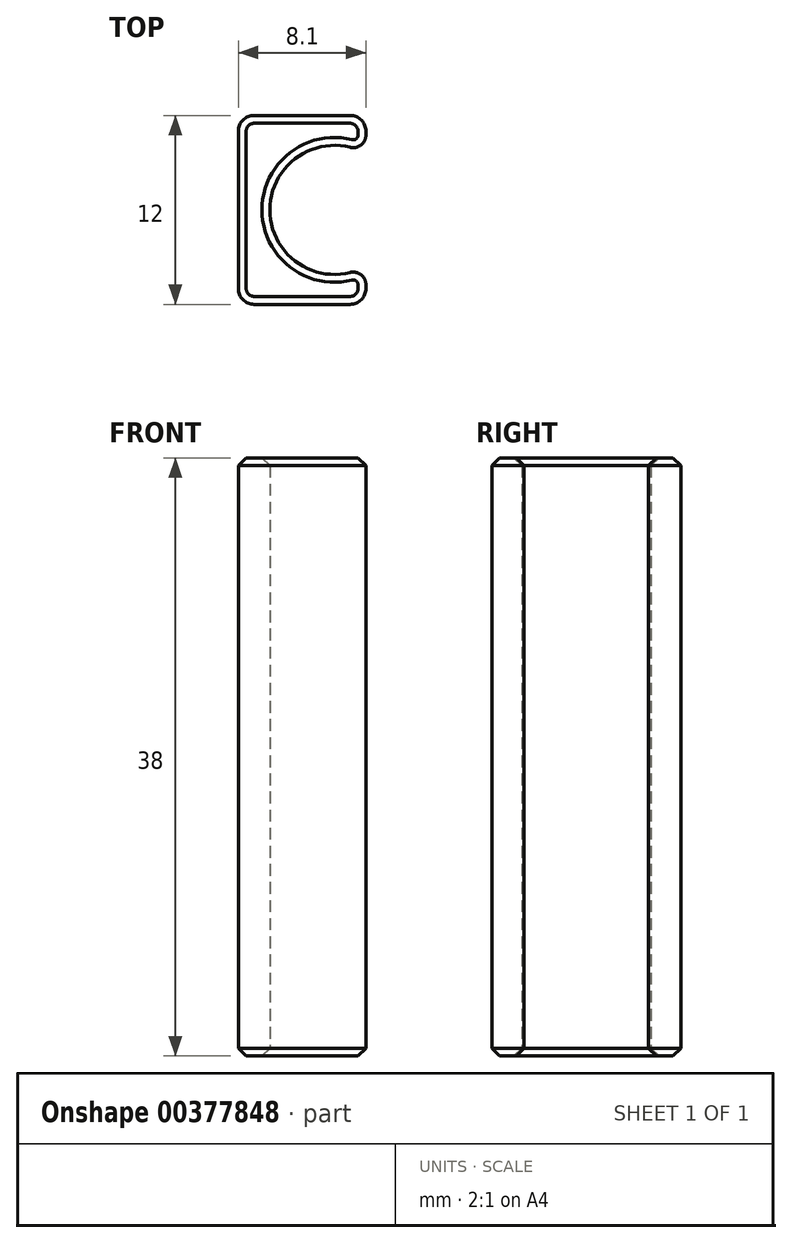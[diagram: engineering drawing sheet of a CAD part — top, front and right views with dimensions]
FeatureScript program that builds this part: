
annotation { "Feature Type Name" : "Feature", "Feature Type Description" : "" }
export const myFeature = defineFeature(function(context is Context, id is Id, definition is map)
    precondition{}
    {
        {
            var Q0;
            Q0=qCreatedBy(makeId("Top.planeOp"),FACE);
            var sketch = newSketch(context, id + "F0", { "sketchPlane" : qUnion([Q0])});
            skLineSegment(sketch, "E0.bottom", {"start": v(4.05, -6) * mm, "end": v(-4.05, -6) * mm});
            skLineSegment(sketch, "E0.top", {"start": v(4.05, 6) * mm, "end": v(-4.05, 6) * mm});
            skLineSegment(sketch, "E0.left", {"start": v(4.05, -6) * mm, "end": v(4.05, -3.58) * mm});
            skLineSegment(sketch, "E0.right", {"start": v(-4.05, -6) * mm, "end": v(-4.05, 6) * mm});
            skPoint(sketch, "E0.middle", {"position": v(0, 0) * mm});
            skArc(sketch, "E1", {"start": v(4.05, 3.58) * mm, "mid": v(-2.05, 0) * mm, "end": v(4.05, -3.58) * mm});
            skPoint(sketch, "E2", {"position": v(4.05, 0) * mm});
            skLineSegment(sketch, "E3.trimOffspring", {"start": v(4.05, 3.58) * mm, "end": v(4.05, 6) * mm});
            skSolve(sketch);
        }
        {
            var Q0;
            Q0 = qSketchRegion(id + "F0", true);
            extrude(context, id + "F1", {"entities" : qUnion([Q0]), "depth" : 38 * mm});
        }
        {
            var Q0;
            Q0=makeQuery(id+"F1.opExtrude","SWEPT_EDGE",EDGE,{"disambiguationData":[OSD([sQuery(id+"F0.wireOp",EDGE,"E1"),sQuery(id+"F0.wireOp",EDGE,"E3.trimOffspring")])]});
            var Q1;
            Q1=makeQuery(id+"F1.opExtrude","SWEPT_EDGE",EDGE,{"disambiguationData":[OSD([sQuery(id+"F0.wireOp",EDGE,"E0.left"),sQuery(id+"F0.wireOp",EDGE,"E1")])]});
            fillet(context, id + "F2", {"entities" : qUnion([Q0, Q1]), "radius" : .8 * mm, "tangentPropagation" : true, "allowEdgeOverflow" : false});
        }
        {
            var Q0;
            Q0=makeQuery(id+"F1.opExtrude","SWEPT_EDGE",EDGE,{"disambiguationData":[OSD([sQuery(id+"F0.wireOp",EDGE,"E0.top"),sQuery(id+"F0.wireOp",EDGE,"E3.trimOffspring")])]});
            var Q1;
            Q1=makeQuery(id+"F1.opExtrude","SWEPT_EDGE",EDGE,{"disambiguationData":[OSD([sQuery(id+"F0.wireOp",EDGE,"E0.bottom"),sQuery(id+"F0.wireOp",EDGE,"E0.left")])]});
            var Q2;
            Q2=makeQuery(id+"F1.opExtrude","SWEPT_EDGE",EDGE,{"disambiguationData":[OSD([sQuery(id+"F0.wireOp",EDGE,"E0.bottom"),sQuery(id+"F0.wireOp",EDGE,"E0.right")])]});
            var Q3;
            Q3=makeQuery(id+"F1.opExtrude","SWEPT_EDGE",EDGE,{"disambiguationData":[OSD([sQuery(id+"F0.wireOp",EDGE,"E0.top"),sQuery(id+"F0.wireOp",EDGE,"E0.right")])]});
            fillet(context, id + "F3", {"entities" : qUnion([Q0, Q1, Q2, Q3]), "radius" : 1 * mm, "tangentPropagation" : true, "allowEdgeOverflow" : false});
        }
        {
            var Q0;
            Q0=makeQuery(id+"F1.opExtrude","CAP_EDGE",EDGE,{"disambiguationData":[OSD([sQuery(id+"F0.wireOp",EDGE,"E1")])],"isStart":false});
            var Q1;
            Q1=makeQuery(id+"F1.opExtrude","CAP_EDGE",EDGE,{"disambiguationData":[OSD([sQuery(id+"F0.wireOp",EDGE,"E1")])],"isStart":true});
            chamfer(context, id + "F4", {"entities" : qUnion([Q0, Q1]), "width" : .5 * mm, "tangentPropagation" : true});
        }
    });
